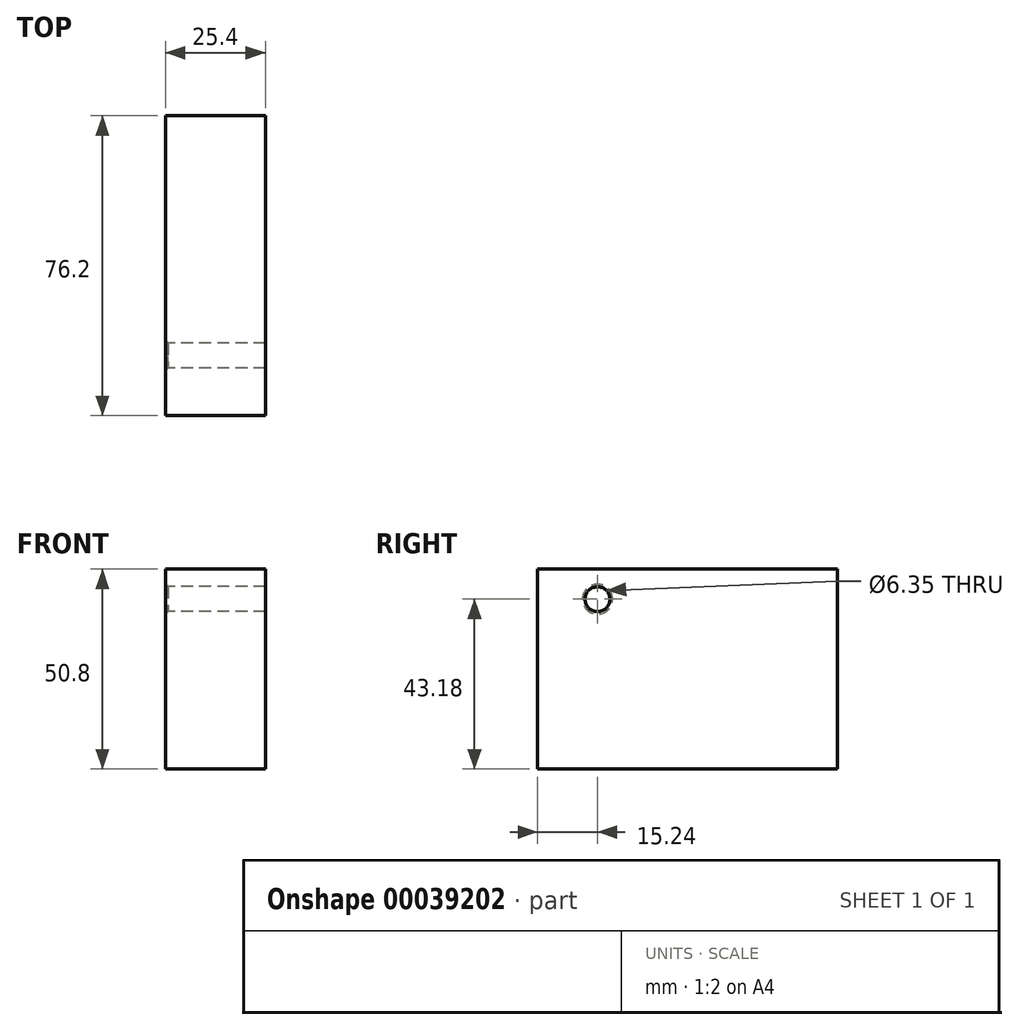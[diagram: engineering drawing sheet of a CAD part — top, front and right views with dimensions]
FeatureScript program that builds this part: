
annotation { "Feature Type Name" : "Feature", "Feature Type Description" : "" }
export const myFeature = defineFeature(function(context is Context, id is Id, definition is map)
    precondition{}
    {
        {
            var Q0;
            Q0=qCreatedBy(makeId("Right.planeOp"),FACE);
            var sketch = newSketch(context, id + "F0", { "sketchPlane" : qUnion([Q0])});
            skLineSegment(sketch, "E0.bottom", {"start": v(0, 0) * mm, "end": v(76.2, 0) * mm});
            skLineSegment(sketch, "E0.top", {"start": v(0, 50.8) * mm, "end": v(76.2, 50.8) * mm});
            skLineSegment(sketch, "E0.left", {"start": v(0, 0) * mm, "end": v(0, 50.8) * mm});
            skLineSegment(sketch, "E0.right", {"start": v(76.2, 0) * mm, "end": v(76.2, 50.8) * mm});
            skPoint(sketch, "E1", {"position": v(15.24, 43.18) * mm});
            skSolve(sketch);
        }
        {
            var Q0;
            Q0=makeQuery(id+"F0.imprint","IMPRINT",FACE,{"disambiguationData":[TD([[makeQuery(id+"F0.imprint","IMPRINT",EDGE,{"derivedFrom":sQuery(id+"F0.wireOp",EDGE,"E0.bottom")}),1.0]])]});
            extrude(context, id + "F1", {"entities" : qUnion([Q0]), "depth" : 25.4 * mm});
        }
        {
            var Q0;
            Q0=sQuery(id+"F0.wireOp",VERTEX,"E1");
            var Q1;
            Q1=makeQuery(id+"F1.opExtrude","SWEPT_BODY",BODY,{"disambiguationData":[OSD([sQuery(id+"F0.wireOp",EDGE,"E0.bottom"),sQuery(id+"F0.wireOp",EDGE,"E0.top"),sQuery(id+"F0.wireOp",EDGE,"E0.left"),sQuery(id+"F0.wireOp",EDGE,"E0.right")])]});
            hole(context, id + "F2", {"style" : HoleStyle.C_SINK, "holeDiameter" : 6.35 * mm, "cSinkDiameter" : 7.62 * mm, "endStyle" : HoleEndStyle.THROUGH, "oppositeDirection" : true, "locations" : qUnion([Q0]), "scope" : qUnion([Q1]), "cSinkAngle" : 90 * degree});
        }
    });
